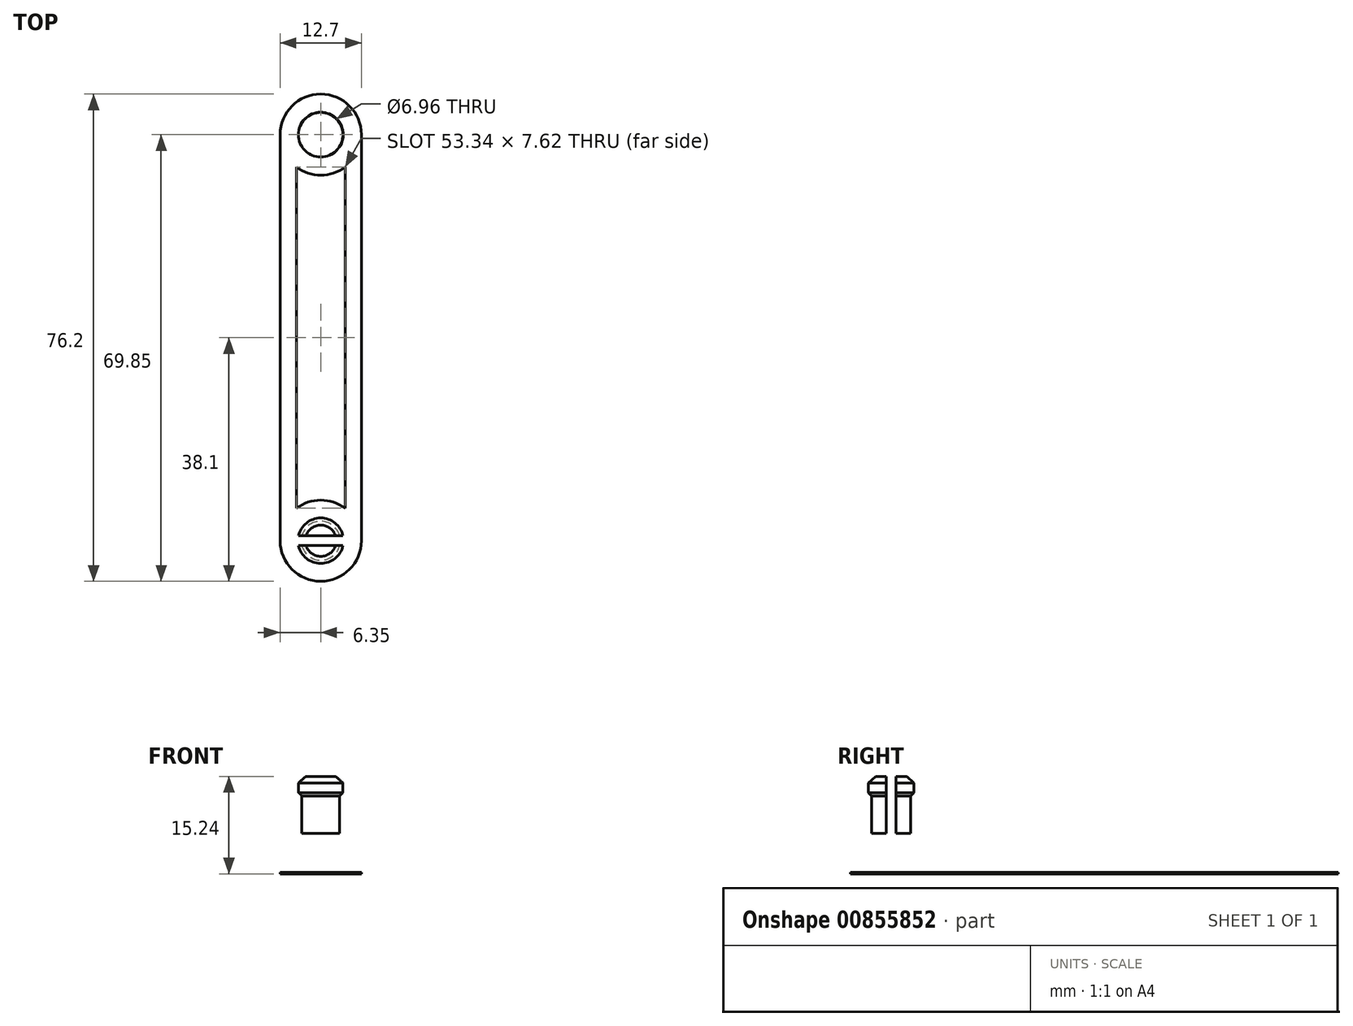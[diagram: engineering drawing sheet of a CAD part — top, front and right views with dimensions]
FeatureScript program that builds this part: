
annotation { "Feature Type Name" : "Feature", "Feature Type Description" : "" }
export const myFeature = defineFeature(function(context is Context, id is Id, definition is map)
    precondition{}
    {
        {
            assignVariable(context, id + "F0", {"name" : "ShaftDiameter", "anyValue" : 0.24});
        }
        {
            assignVariable(context, id + "F1", {"name" : "Thickness", "anyValue" : .25});
        }
        {
            var Q0;
            Q0=qCreatedBy(makeId("Top.planeOp"),FACE);
            var sketch = newSketch(context, id + "F2", { "sketchPlane" : qUnion([Q0])});
            skCircle(sketch, "E0", {"center": v(0, 0) * mm, "radius": 6.35 * mm});
            skCircle(sketch, "E1", {"center": v(0, -63.5) * mm, "radius": 6.35 * mm});
            skLineSegment(sketch, "E2", {"start": v(0, 41.86) * mm, "end": v(0, -77.4) * mm, "construction": true});
            skLineSegment(sketch, "E3", {"start": v(-6.35, 0) * mm, "end": v(-6.35, -63.5) * mm});
            skLineSegment(sketch, "E4", {"start": v(6.35, 0) * mm, "end": v(6.35, -63.5) * mm});
            skLineSegment(sketch, "E5", {"start": v(3.8, -5.08) * mm, "end": v(3.81, -58.42) * mm});
            skLineSegment(sketch, "E6.MirrorCS", {"start": v(-3.8, -5.08) * mm, "end": v(-3.81, -58.42) * mm});
            skCircle(sketch, "E7", {"center": v(0, 0) * mm, "radius": 3.48 * mm});
            skSolve(sketch);
        }
        {
            var Q0;
            {var subQ0=sQuery(id+"F2.wireOp",EDGE,"E3");Q0=makeQuery(id+"F2.imprint","IMPRINT",FACE,{"disambiguationData":[TD([[makeQuery(id+"F2.imprint","IMPRINT",EDGE,{"derivedFrom":subQ0}),1.0]])]});}
            var Q1;
            Q1=makeQuery(id+"F2.imprint","IMPRINT",FACE,{"disambiguationData":[TD([[makeQuery(id+"F2.imprint","IMPRINT",EDGE,{"derivedFrom":sQuery(id+"F2.wireOp",EDGE,"E7")}),-1.0]])]});
            var Q2;
            {var subQ0=sQuery(id+"F2.wireOp",EDGE,"E4");Q2=makeQuery(id+"F2.imprint","IMPRINT",FACE,{"disambiguationData":[TD([[makeQuery(id+"F2.imprint","IMPRINT",EDGE,{"derivedFrom":subQ0}),-1.0]])]});}
            var Q3;
            Q3=makeQuery(id+"F2.imprint","IMPRINT",FACE,{"disambiguationData":[TD([[makeQuery(id+"F2.imprint","IMPRINT",EDGE,{"derivedFrom":sQuery(id+"F2.wireOp",EDGE,"4J6F0PSJ-IIou-Oit7-jF6V-CEa8EtvErhOJ")}),-1.0]])]});
            var Q4;
            {var subQ0=sQuery(id+"F2.wireOp",EDGE,"E1");var subQ1=makeQuery(id+"F2.imprint","INTERSECT",VERTEX,{"derivedFrom":[subQ0,sQuery(id+"F2.wireOp",EDGE,"E4")]});Q4=makeQuery(id+"F2.imprint","IMPRINT",FACE,{"disambiguationData":[TD([[makeQuery(id+"F2.imprint","IMPRINT",EDGE,{"disambiguationData":[TD([[subQ1,-1.0]])],"derivedFrom":subQ0}),1.0]])]});}
            extrude(context, id + "F3", {"entities" : qUnion([Q0, Q1, Q2, Q3, Q4]), "depth" : (getVariable(context, 'Thickness')) * mm, "offsetDistance" : 25.4 * mm});
        }
        {
            var Q0;
            Q0=qCreatedBy(makeId("Right.planeOp"),FACE);
            var sketch = newSketch(context, id + "F4", { "sketchPlane" : qUnion([Q0])});
            skLineSegment(sketch, "E8.0.0", {"start": v(0, 6.35) * mm, "end": v(-63.5, 6.35) * mm});
            skLineSegment(sketch, "E8.0.1", {"start": v(-63.5, 6.35) * mm, "end": v(-69.85, 6.35) * mm});
            skLineSegment(sketch, "E8.0.2", {"start": v(-63.5, 6.35) * mm, "end": v(0, 6.35) * mm});
            skLineSegment(sketch, "E8.0.3", {"start": v(0, 6.35) * mm, "end": v(6.35, 6.35) * mm});
            skLineSegment(sketch, "E9.0", {"start": v(-3.48, 6.35) * mm, "end": v(3.48, 6.35) * mm});
            skLineSegment(sketch, "E10", {"start": v(-63.5, 15.76) * mm, "end": v(-63.5, 0) * mm, "construction": true});
            skLineSegment(sketch, "E11", {"start": v(-66.55, 6.35) * mm, "end": v(-66.55, 12.2) * mm});
            skLineSegment(sketch, "E12", {"start": v(-66.55, 12.2) * mm, "end": v(-67.06, 12.7) * mm});
            skLineSegment(sketch, "E13", {"start": v(-67.06, 12.7) * mm, "end": v(-67.06, 14.22) * mm});
            skLineSegment(sketch, "E14", {"start": v(-67.06, 14.22) * mm, "end": v(-65.94, 15.24) * mm});
            skLineSegment(sketch, "E15", {"start": v(-65.94, 15.24) * mm, "end": v(-63.5, 15.24) * mm});
            skLineSegment(sketch, "E16", {"start": v(-63.5, 15.24) * mm, "end": v(-63.5, 6.35) * mm});
            skSolve(sketch);
        }
        {
            var Q0;
            {var subQ0=sQuery(id+"F4.wireOp",EDGE,"E11");Q0=makeQuery(id+"F4.imprint","IMPRINT",FACE,{"disambiguationData":[TD([[makeQuery(id+"F4.imprint","IMPRINT",EDGE,{"derivedFrom":subQ0}),-1.0]])]});}
            var Q1;
            Q1=sQuery(id+"F4.wireOp",EDGE,"E10");
            revolve(context, id + "F5", {"operationType" : NewBodyOperationType.ADD, "surfaceOperationType" : NewSurfaceOperationType.NEW, "entities" : qUnion([Q0]), "axis" : qUnion([Q1]), "revolveType" : RevolveType.FULL});
        }
        {
            var Q0;
            Q0=makeQuery(id+"F5.opRevolve","SWEPT_FACE",FACE,{"disambiguationData":[OSD([sQuery(id+"F4.wireOp",EDGE,"E15")])]});
            var sketch = newSketch(context, id + "F6", { "sketchPlane" : qUnion([Q0])});
            skCircle(sketch, "E17.0", {"center": v(0, -63.5) * mm, "radius": 3.56 * mm});
            skLineSegment(sketch, "E18", {"start": v(-3.56, -63.5) * mm, "end": v(3.56, -63.5) * mm, "construction": true});
            skLineSegment(sketch, "E19", {"start": v(-3.47, -62.74) * mm, "end": v(3.47, -62.74) * mm});
            skLineSegment(sketch, "E20", {"start": v(3.47, -64.26) * mm, "end": v(-3.47, -64.26) * mm});
            skSolve(sketch);
        }
        {
            var Q0;
            {var subQ0=sQuery(id+"F6.wireOp",EDGE,"E19");var subQ1=sQuery(id+"F6.wireOp",EDGE,"E17.0");var subQ2=makeQuery(id+"F6.imprint","INTERSECT",VERTEX,{"disambiguationData":[OD(0.0)],"derivedFrom":[subQ1,subQ0]});Q0=makeQuery(id+"F6.imprint","IMPRINT",FACE,{"disambiguationData":[TD([[makeQuery(id+"F6.imprint","IMPRINT",EDGE,{"disambiguationData":[TD([[subQ2,-1.0]])],"derivedFrom":subQ1}),1.0]])]});}
            var Q1;
            {var subQ0=sQuery(id+"F6.wireOp",EDGE,"E19");var subQ1=makeQuery(id+"F5.opRevolve","SWEPT_EDGE",EDGE,{"disambiguationData":[OSD([sQuery(id+"F4.wireOp",EDGE,"E14"),sQuery(id+"F4.wireOp",EDGE,"E15")])]});var subQ2=makeQuery(id+"F6.imprint","INTERSECT",VERTEX,{"disambiguationData":[OD(0.0)],"derivedFrom":[subQ1,subQ0]});Q1=makeQuery(id+"F6.imprint","IMPRINT",FACE,{"disambiguationData":[TD([[makeQuery(id+"F6.imprint","IMPRINT",EDGE,{"disambiguationData":[TD([[subQ2,-1.0]])],"derivedFrom":subQ0}),-1.0]])]});}
            var Q2;
            {var subQ0=sQuery(id+"F6.wireOp",EDGE,"E19");var subQ1=sQuery(id+"F6.wireOp",EDGE,"E17.0");var subQ2=makeQuery(id+"F6.imprint","INTERSECT",VERTEX,{"disambiguationData":[OD(1.0)],"derivedFrom":[subQ1,subQ0]});Q2=makeQuery(id+"F6.imprint","IMPRINT",FACE,{"disambiguationData":[TD([[makeQuery(id+"F6.imprint","IMPRINT",EDGE,{"disambiguationData":[TD([[subQ2,1.0]])],"derivedFrom":subQ1}),1.0]])]});}
            var Q3;
            Q3=makeQuery(id+"F3.opExtrude","CAP_FACE",FACE,{"disambiguationData":[OSD([sQuery(id+"F2.wireOp",EDGE,"E0"),sQuery(id+"F2.wireOp",EDGE,"E1"),sQuery(id+"F2.wireOp",EDGE,"E3"),sQuery(id+"F2.wireOp",EDGE,"E4"),sQuery(id+"F2.wireOp",EDGE,"E5"),sQuery(id+"F2.wireOp",EDGE,"E6.MirrorCS"),sQuery(id+"F2.wireOp",EDGE,"E7")])],"isStart":false});
            extrude(context, id + "F7", {"entities" : qUnion([Q0, Q1, Q2]), "operationType" : NewBodyOperationType.REMOVE, "endBound" : BoundingType.UP_TO_SURFACE, "oppositeDirection" : true, "depth" : 25.4 * mm, "endBoundEntityFace" : qUnion([Q3]), "offsetDistance" : 25.4 * mm});
        }
        {
            var Q0;
            Q0=makeQuery(id+"F3.opExtrude","CAP_EDGE",EDGE,{"disambiguationData":[OSD([sQuery(id+"F2.wireOp",EDGE,"E7")])],"isStart":false});
            var Q1;
            Q1=makeQuery(id+"F3.opExtrude","CAP_EDGE",EDGE,{"disambiguationData":[OSD([sQuery(id+"F2.wireOp",EDGE,"E7")])],"isStart":true});
            chamfer(context, id + "F8", {"entities" : qUnion([Q0, Q1]), "chamferType" : ChamferType.OFFSET_ANGLE, "width" : (.1 * getVariable(context, 'ShaftDiameter')) * mm, "oppositeDirection" : false, "angle" : 45 * degree, "tangentPropagation" : true});
        }
    });
